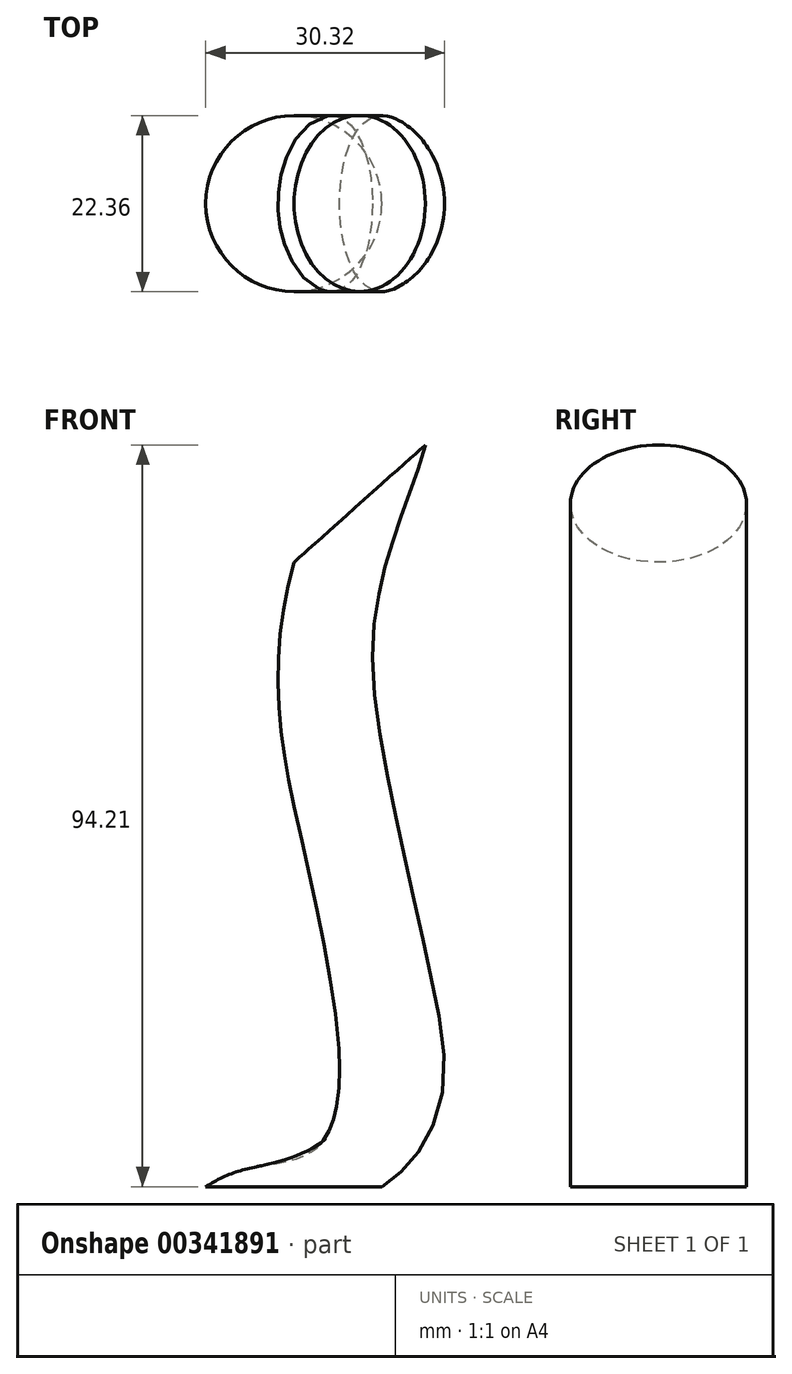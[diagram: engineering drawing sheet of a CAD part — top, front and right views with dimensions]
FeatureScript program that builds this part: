
annotation { "Feature Type Name" : "Feature", "Feature Type Description" : "" }
export const myFeature = defineFeature(function(context is Context, id is Id, definition is map)
    precondition{}
    {
        {
            var Q0;
            Q0=qCreatedBy(makeId("Top.planeOp"),FACE);
            var sketch = newSketch(context, id + "F0", { "sketchPlane" : qUnion([Q0])});
            skCircle(sketch, "E0", {"center": v(-62.28, 52.52) * mm, "radius": 11.18 * mm});
            skSolve(sketch);
        }
        {
            var Q0;
            Q0=sQuery(id+"F0.wireOp",VERTEX,"E0.center");
            var Q1;
            Q1=qCreatedBy(makeId("Front.planeOp"),FACE);
            cPlane(context, id + "F1", {"entities" : qUnion([Q0, Q1]), "cplaneType" : CPlaneType.PLANE_POINT, "offset" : 25.4 * mm, "width" : 152.4 * mm, "height" : 152.4 * mm});
        }
        {
            var Q0;
            Q0=qCreatedBy(id+"F1.planeOp",FACE);
            var sketch = newSketch(context, id + "F2", { "sketchPlane" : qUnion([Q0])});
            skFitSpline(sketch, "E1", {"points": [v(-62.62, 0) * mm, v(-51.8, 12.5) * mm, v(-57.55, 59.5) * mm, v(-54.17, 86.54) * mm], "startDerivative": vector(55.92, 35.8) * mm, "endDerivative": vector(20.35, 72.92) * mm});
            skSolve(sketch);
        }
        {
            var Q0;
            Q0=makeQuery(id+"F0.imprint","IMPRINT",FACE,{"disambiguationData":[TD([[makeQuery(id+"F0.imprint","IMPRINT",EDGE,{"derivedFrom":sQuery(id+"F0.wireOp",EDGE,"E0")}),1.0]])]});
            var Q1;
            Q1=sQuery(id+"F2.wireOp",EDGE,"E1");
            sweep(context, id + "F3", {"profiles" : qUnion([Q0]), "path" : qUnion([Q1])});
        }
        {
            var Q0;
            Q0=qCreatedBy(id+"F1.planeOp",FACE);
            var sketch = newSketch(context, id + "F4", { "sketchPlane" : qUnion([Q0])});
            skLineSegment(sketch, "E2", {"start": v(-56.41, 76.47) * mm, "end": v(-56.41, 141.37) * mm});
            skSolve(sketch);
        }
        {
            var Q0;
            Q0=qCreatedBy(id+"F1.planeOp",FACE);
            var sketch = newSketch(context, id + "F5", { "sketchPlane" : qUnion([Q0])});
            skFitSpline(sketch, "E3", {"points": [v(-56.05, 141.74) * mm, v(-10.95, 142.47) * mm, v(-20.85, 95.54) * mm, v(-56.41, 76.1) * mm], "startDerivative": vector(171.6, 43.62) * mm, "endDerivative": vector(-122.5, -33) * mm});
            skSolve(sketch);
        }
        {
            var Q0;
            Q0=sQuery(id+"F5.wireOp",EDGE,"E3");
            var Q1;
            Q1=sQuery(id+"F4.wireOp",EDGE,"E2");
            revolve(context, id + "F6", {"bodyType" : ToolBodyType.SURFACE, "surfaceEntities" : qUnion([Q0]), "axis" : qUnion([Q1]), "revolveType" : RevolveType.FULL});
        }
    });
